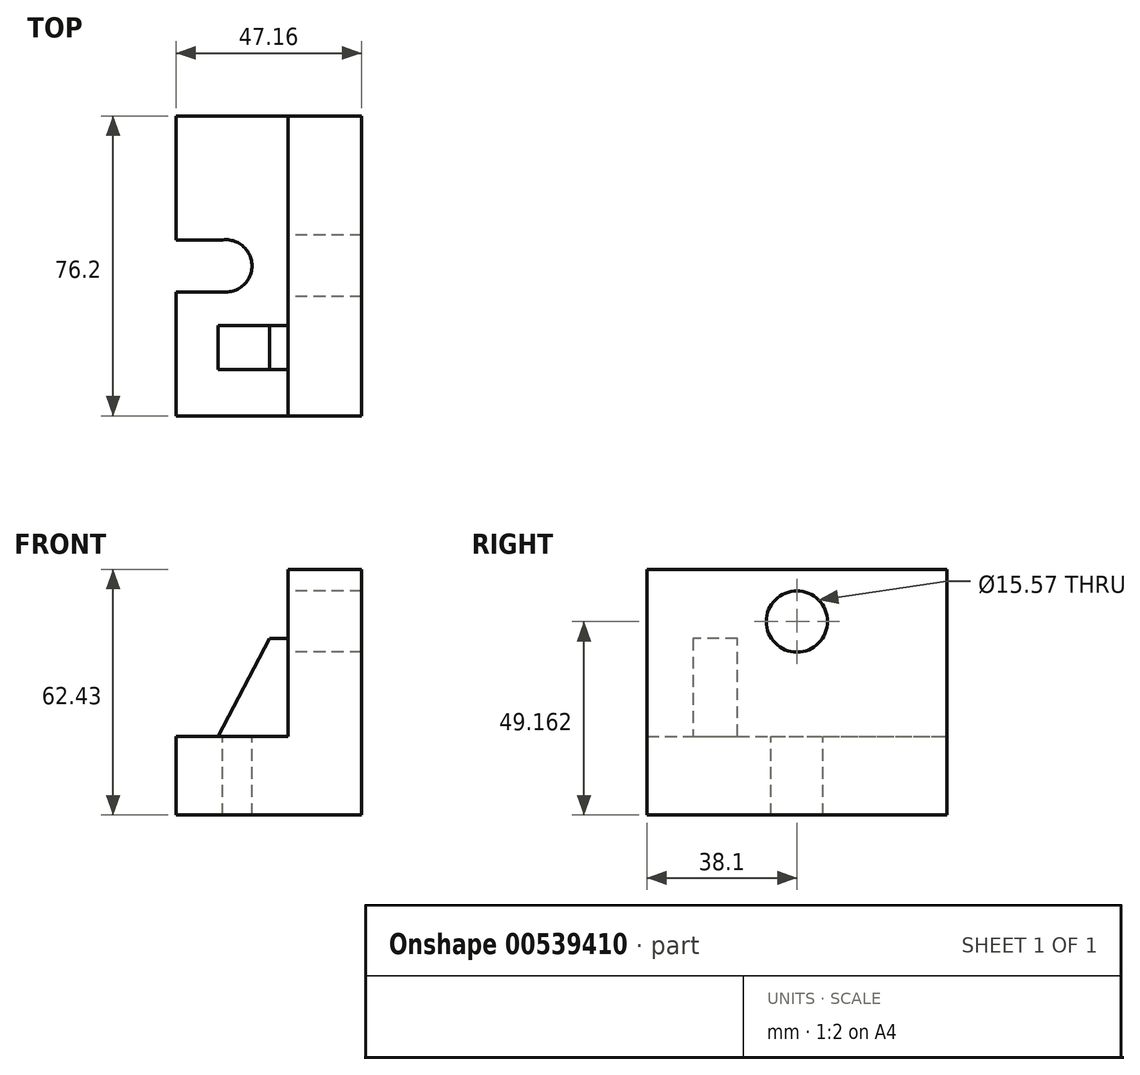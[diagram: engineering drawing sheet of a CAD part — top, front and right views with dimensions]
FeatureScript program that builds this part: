
annotation { "Feature Type Name" : "Feature", "Feature Type Description" : "" }
export const myFeature = defineFeature(function(context is Context, id is Id, definition is map)
    precondition{}
    {
        {
            var Q0;
            Q0=qCreatedBy(makeId("Front.planeOp"),FACE);
            var sketch = newSketch(context, id + "F0", { "sketchPlane" : qUnion([Q0])});
            skLineSegment(sketch, "E0", {"start": v(0, 0) * mm, "end": v(0, 62.43) * mm});
            skLineSegment(sketch, "E1", {"start": v(0, 62.43) * mm, "end": v(-18.69, 62.43) * mm});
            skLineSegment(sketch, "E2", {"start": v(-18.69, 62.43) * mm, "end": v(-18.69, 20.02) * mm});
            skLineSegment(sketch, "E3", {"start": v(-18.69, 20.02) * mm, "end": v(-47.16, 20.02) * mm});
            skLineSegment(sketch, "E4", {"start": v(-47.16, 20.02) * mm, "end": v(-47.16, 0) * mm});
            skLineSegment(sketch, "E5", {"start": v(-47.16, 0) * mm, "end": v(0, 0) * mm});
            skSolve(sketch);
        }
        {
            var Q0;
            Q0 = qSketchRegion(id + "F0", true);
            extrude(context, id + "F1", {"entities" : qUnion([Q0]), "endBound" : BoundingType.SYMMETRIC, "depth" : 76.2 * mm, "offsetDistance" : 25.4 * mm});
        }
        {
            var Q0;
            Q0=makeQuery(id+"F1.opExtrude","SWEPT_FACE",FACE,{"disambiguationData":[OSD([sQuery(id+"F0.wireOp",EDGE,"E3")])]});
            var sketch = newSketch(context, id + "F2", { "sketchPlane" : qUnion([Q0])});
            skCircle(sketch, "E6", {"center": v(-34.5, 0) * mm, "radius": 6.64 * mm});
            skLineSegment(sketch, "E7", {"start": v(-33.68, 6.6) * mm, "end": v(-47.16, 6.6) * mm});
            skLineSegment(sketch, "E8", {"start": v(-34.5, -6.64) * mm, "end": v(-47.16, -6.64) * mm});
            skLineSegment(sketch, "E9", {"start": v(-47.16, 6.6) * mm, "end": v(-47.16, -6.64) * mm});
            skSolve(sketch);
        }
        {
            var Q0;
            Q0 = qSketchRegion(id + "F2", true);
            extrude(context, id + "F3", {"entities" : qUnion([Q0]), "operationType" : NewBodyOperationType.REMOVE, "endBound" : BoundingType.THROUGH_ALL, "oppositeDirection" : true, "depth" : 30.23 * mm, "offsetDistance" : 25.4 * mm});
        }
        {
            var Q0;
            Q0=makeQuery(id+"F1.opExtrude","SWEPT_FACE",FACE,{"disambiguationData":[OSD([sQuery(id+"F0.wireOp",EDGE,"E2")])]});
            var sketch = newSketch(context, id + "F4", { "sketchPlane" : qUnion([Q0])});
            skCircle(sketch, "E10", {"center": v(0, 49.16) * mm, "radius": 7.78 * mm});
            skSolve(sketch);
        }
        {
            var Q0;
            Q0=makeQuery(id+"F4.imprint","IMPRINT",FACE,{"disambiguationData":[TD([[makeQuery(id+"F4.imprint","IMPRINT",EDGE,{"derivedFrom":sQuery(id+"F4.wireOp",EDGE,"E10")}),1.0]])]});
            var Q1;
            Q1=sQuery(id+"F4.wireOp",EDGE,"E10");
            extrude(context, id + "F5", {"entities" : qUnion([Q0]), "operationType" : NewBodyOperationType.REMOVE, "surfaceEntities" : qUnion([Q1]), "endBound" : BoundingType.THROUGH_ALL, "oppositeDirection" : true, "depth" : 102.1 * mm, "offsetDistance" : 25.4 * mm});
        }
        {
            var Q0;
            Q0=makeQuery(id+"F1.opExtrude","SWEPT_FACE",FACE,{"disambiguationData":[OSD([sQuery(id+"F0.wireOp",EDGE,"E2")])]});
            var sketch = newSketch(context, id + "F6", { "sketchPlane" : qUnion([Q0])});
            skLineSegment(sketch, "E11", {"start": v(15.15, 20.02) * mm, "end": v(15.15, 44.8) * mm});
            skLineSegment(sketch, "E12", {"start": v(15.15, 44.8) * mm, "end": v(26.36, 44.8) * mm});
            skLineSegment(sketch, "E13", {"start": v(26.36, 44.8) * mm, "end": v(26.36, 20.02) * mm});
            skSolve(sketch);
        }
        {
            var Q0;
            Q0 = qSketchRegion(id + "F6", true);
            var Q1;
            {var subQ0=sQuery(id+"F6.wireOp",EDGE,"E11");Q1=makeQuery(id+"F6.imprint","IMPRINT",FACE,{"disambiguationData":[TD([[makeQuery(id+"F6.imprint","IMPRINT",EDGE,{"derivedFrom":subQ0}),-1.0]])]});}
            extrude(context, id + "F7", {"entities" : qUnion([Q0, Q1]), "operationType" : NewBodyOperationType.ADD, "depth" : 17.78 * mm, "offsetDistance" : 25.4 * mm});
        }
        {
            var Q0;
            Q0=makeQuery(id+"F7.opExtrude","SWEPT_FACE",FACE,{"disambiguationData":[OSD([sQuery(id+"F6.wireOp",EDGE,"E13")])]});
            var sketch = newSketch(context, id + "F8", { "sketchPlane" : qUnion([Q0])});
            skLineSegment(sketch, "E14", {"start": v(-23.35, 44.8) * mm, "end": v(-36.47, 20.02) * mm});
            skLineSegment(sketch, "E15", {"start": v(-36.47, 20.02) * mm, "end": v(-36.47, 44.8) * mm});
            skLineSegment(sketch, "E16", {"start": v(-36.47, 44.8) * mm, "end": v(-23.35, 44.8) * mm});
            skSolve(sketch);
        }
        {
            var Q0;
            Q0=makeQuery(id+"F8.imprint","IMPRINT",FACE,{"disambiguationData":[TD([[makeQuery(id+"F8.imprint","IMPRINT",EDGE,{"derivedFrom":sQuery(id+"F8.wireOp",EDGE,"E14")}),-1.0]])]});
            extrude(context, id + "F9", {"entities" : qUnion([Q0]), "operationType" : NewBodyOperationType.REMOVE, "endBound" : BoundingType.THROUGH_ALL, "oppositeDirection" : true, "depth" : 25.4 * mm, "offsetDistance" : 25.4 * mm});
        }
    });
